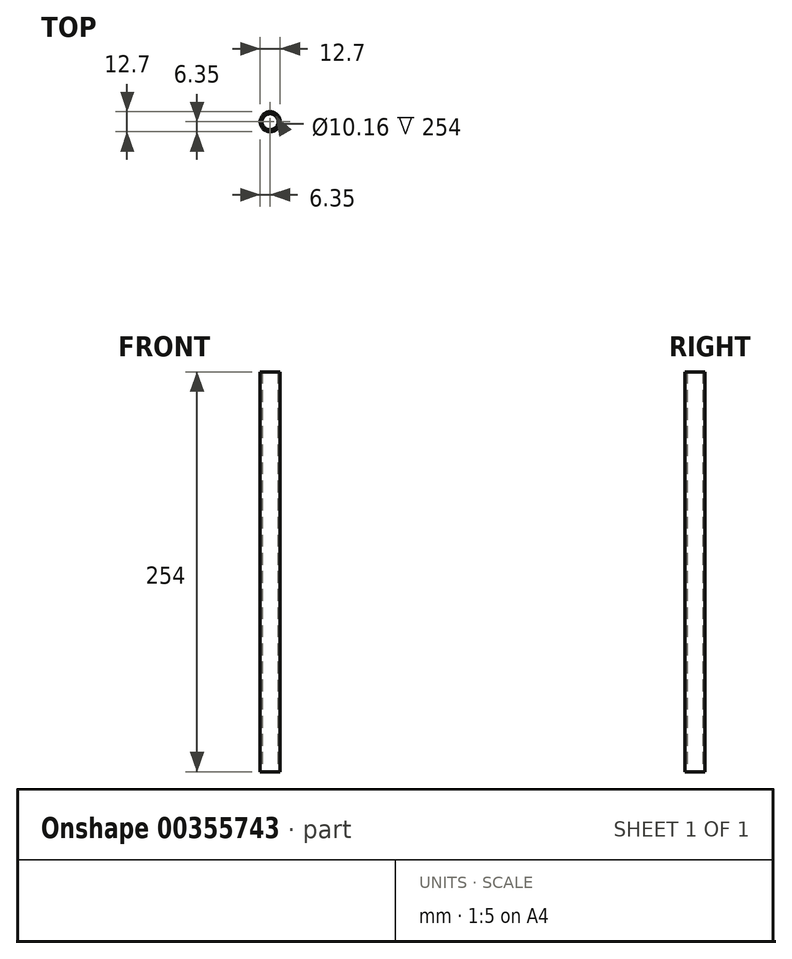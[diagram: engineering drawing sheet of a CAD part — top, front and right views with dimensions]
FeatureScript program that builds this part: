
annotation { "Feature Type Name" : "Feature", "Feature Type Description" : "" }
export const myFeature = defineFeature(function(context is Context, id is Id, definition is map)
    precondition{}
    {
        {
            var Q0;
            Q0=qCreatedBy(makeId("Top.planeOp"),FACE);
            var sketch = newSketch(context, id + "F0", { "sketchPlane" : qUnion([Q0])});
            skCircle(sketch, "E0", {"center": v(0, 0) * mm, "radius": 5.08 * mm});
            skCircle(sketch, "E1", {"center": v(0, 0) * mm, "radius": 6.35 * mm});
            skSolve(sketch);
        }
        {
            var Q0;
            Q0 = qSketchRegion(id + "F0", true);
            extrude(context, id + "F1", {"entities" : qUnion([Q0]), "depth" : 254 * mm});
        }
    });
